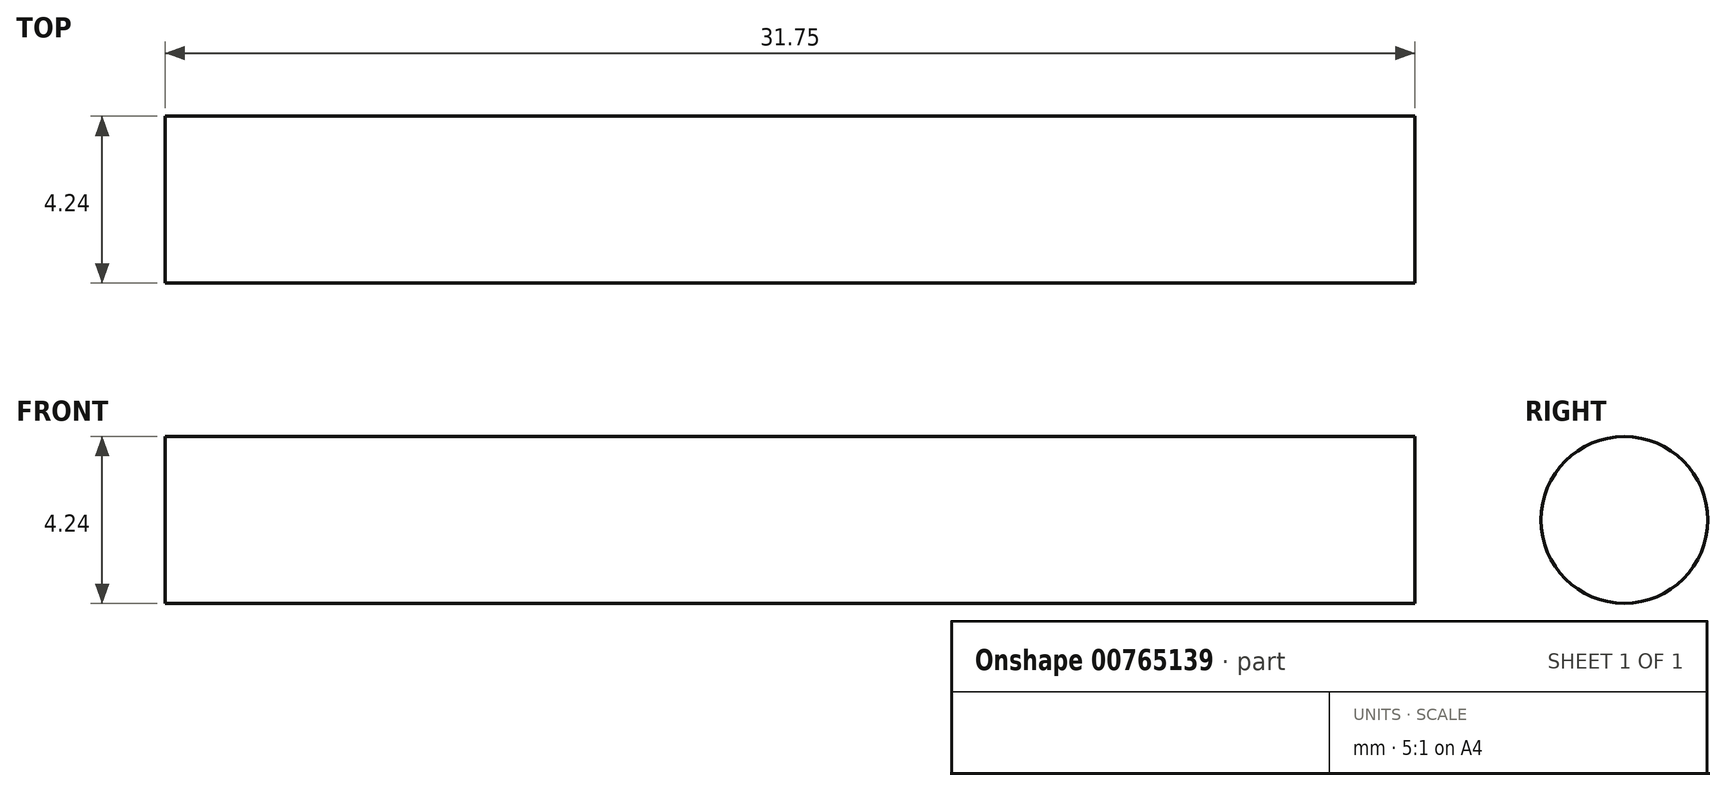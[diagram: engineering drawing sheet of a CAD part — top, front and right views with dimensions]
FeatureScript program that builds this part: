
annotation { "Feature Type Name" : "Feature", "Feature Type Description" : "" }
export const myFeature = defineFeature(function(context is Context, id is Id, definition is map)
    precondition{}
    {
        {
            var Q0;
            Q0=qCreatedBy(makeId("Right.planeOp"),FACE);
            var sketch = newSketch(context, id + "F0", { "sketchPlane" : qUnion([Q0])});
            skCircle(sketch, "E0", {"center": v(0, 0) * mm, "radius": 2.12 * mm});
            skSolve(sketch);
        }
        {
            var Q0;
            Q0=makeQuery(id+"F0.imprint","IMPRINT",FACE,{"disambiguationData":[TD([[makeQuery(id+"F0.imprint","IMPRINT",EDGE,{"derivedFrom":sQuery(id+"F0.wireOp",EDGE,"E0")}),1.0]])]});
            extrude(context, id + "F1", {"entities" : qUnion([Q0]), "depth" : 31.75 * mm, "offsetDistance" : 25.4 * mm});
        }
    });
